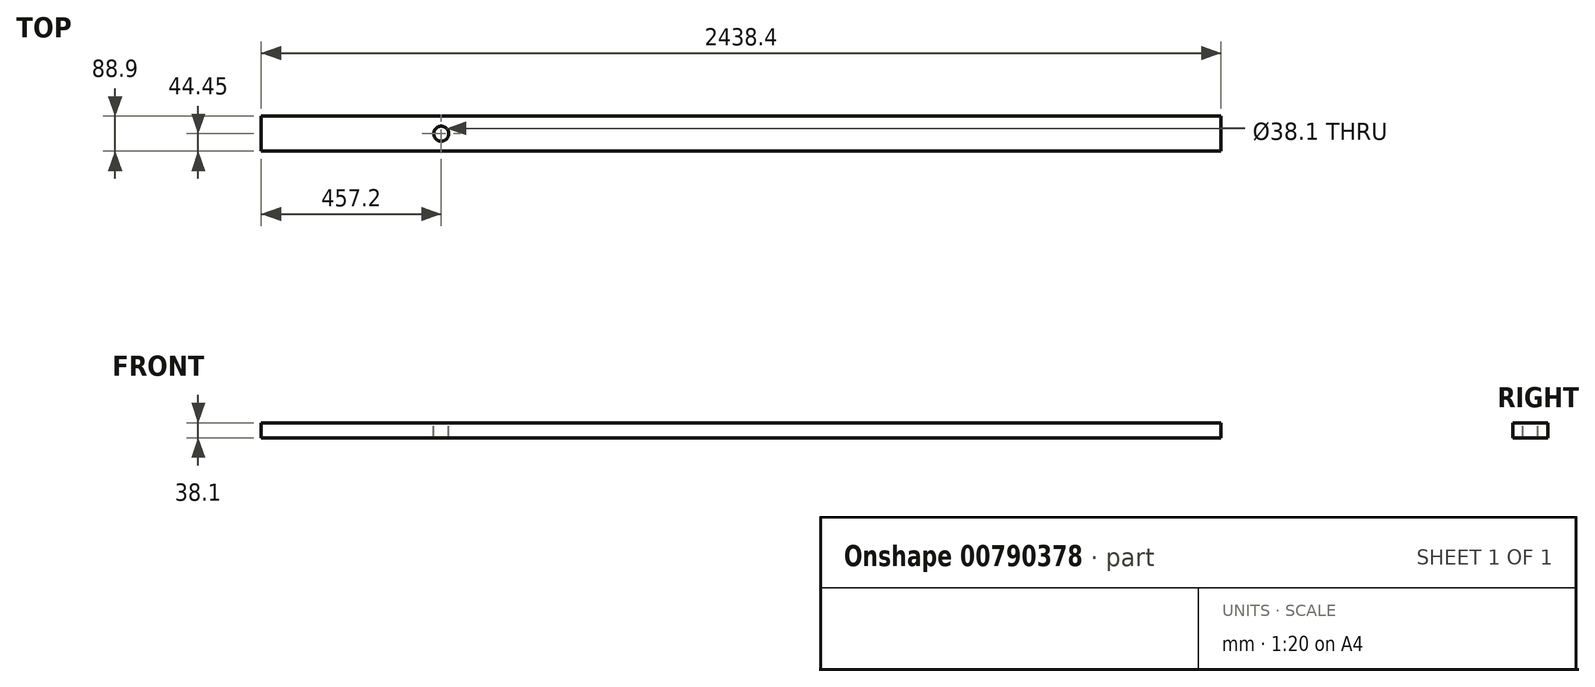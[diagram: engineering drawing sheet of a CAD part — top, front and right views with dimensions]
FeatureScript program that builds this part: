
annotation { "Feature Type Name" : "Feature", "Feature Type Description" : "" }
export const myFeature = defineFeature(function(context is Context, id is Id, definition is map)
    precondition{}
    {
        {
            var Q0;
            Q0=qCreatedBy(makeId("Top.planeOp"),FACE);
            var sketch = newSketch(context, id + "F0", { "sketchPlane" : qUnion([Q0])});
            skLineSegment(sketch, "E0.bottom", {"start": v(0, 0) * mm, "end": v(2438.4, 0) * mm});
            skLineSegment(sketch, "E0.top", {"start": v(0, -88.9) * mm, "end": v(2438.4, -88.9) * mm});
            skLineSegment(sketch, "E0.left", {"start": v(0, 0) * mm, "end": v(0, -88.9) * mm});
            skLineSegment(sketch, "E0.right", {"start": v(2438.4, 0) * mm, "end": v(2438.4, -88.9) * mm});
            skSolve(sketch);
        }
        {
            var Q0;
            Q0=makeQuery(id+"F0.imprint","IMPRINT",FACE,{"disambiguationData":[TD([[makeQuery(id+"F0.imprint","IMPRINT",EDGE,{"derivedFrom":sQuery(id+"F0.wireOp",EDGE,"E0.bottom")}),-1.0]])]});
            extrude(context, id + "F1", {"entities" : qUnion([Q0]), "depth" : 38.1 * mm, "offsetDistance" : 25.4 * mm});
        }
        {
            var Q0;
            Q0=makeQuery(id+"F1.opExtrude","CAP_FACE",FACE,{"disambiguationData":[OSD([sQuery(id+"F0.wireOp",EDGE,"E0.bottom"),sQuery(id+"F0.wireOp",EDGE,"E0.top"),sQuery(id+"F0.wireOp",EDGE,"E0.left"),sQuery(id+"F0.wireOp",EDGE,"E0.right")])],"isStart":false});
            var sketch = newSketch(context, id + "F2", { "sketchPlane" : qUnion([Q0])});
            skLineSegment(sketch, "E1", {"start": v(0, -44.45) * mm, "end": v(457.2, -44.45) * mm});
            skCircle(sketch, "E2", {"center": v(457.2, -44.45) * mm, "radius": 19.05 * mm});
            skSolve(sketch);
        }
        {
            var Q0;
            Q0=makeQuery(id+"F2.imprint","IMPRINT",FACE,{"disambiguationData":[TD([[makeQuery(id+"F2.imprint","IMPRINT",EDGE,{"derivedFrom":sQuery(id+"F2.wireOp",EDGE,"E2")}),1.0]])]});
            extrude(context, id + "F3", {"entities" : qUnion([Q0]), "operationType" : NewBodyOperationType.REMOVE, "oppositeDirection" : true, "depth" : 38.1 * mm, "offsetDistance" : 25.4 * mm});
        }
    });
